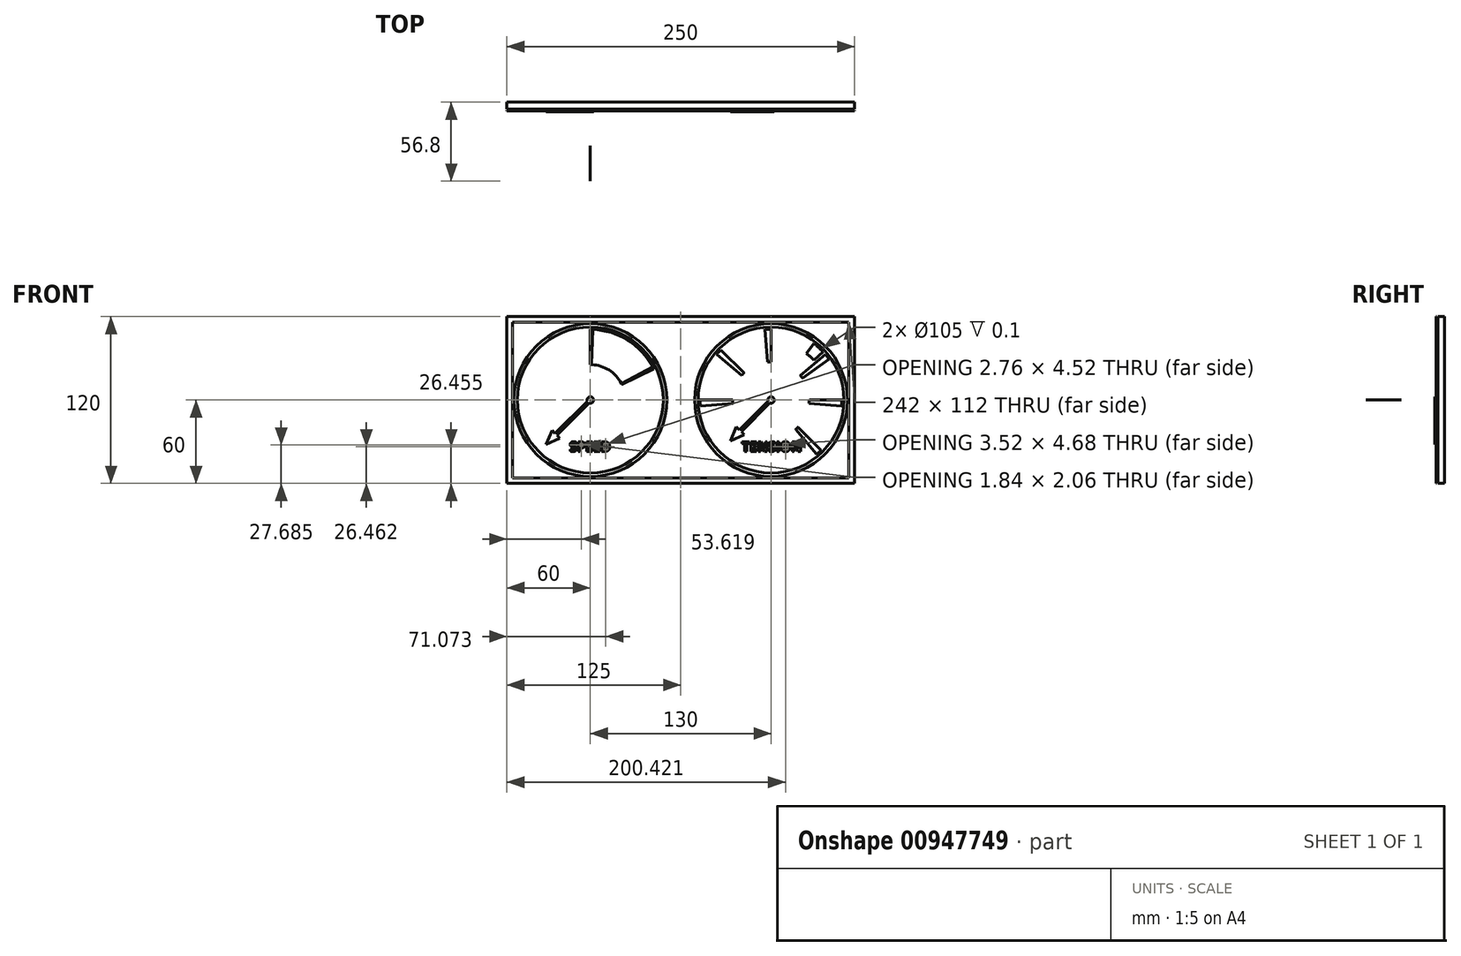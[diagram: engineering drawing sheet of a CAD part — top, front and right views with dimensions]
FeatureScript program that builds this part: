
annotation { "Feature Type Name" : "Feature", "Feature Type Description" : "" }
export const myFeature = defineFeature(function(context is Context, id is Id, definition is map)
    precondition{}
    {
        {
            var Q0;
            Q0=qCreatedBy(makeId("Right.planeOp"),FACE);
            var sketch = newSketch(context, id + "F0", { "sketchPlane" : qUnion([Q0])});
            skLineSegment(sketch, "E0", {"start": v(0, 0) * mm, "end": v(-116.06, 0) * mm, "construction": true});
            skSolve(sketch);
        }
        {
            var Q0;
            Q0=qCreatedBy(makeId("Right.planeOp"),FACE);
            var Q1;
            Q1=sQuery(id+"F0.wireOp",EDGE,"E0");
            cPlane(context, id + "F1", {"entities" : qUnion([Q0, Q1]), "cplaneType" : CPlaneType.LINE_ANGLE, "offset" : 25 * mm, "angle" : 135 * degree, "width" : 150 * mm, "height" : 150 * mm});
        }
        {
            var Q0;
            Q0=qCreatedBy(id+"F1.planeOp",FACE);
            var sketch = newSketch(context, id + "F2", { "sketchPlane" : qUnion([Q0])});
            skLineSegment(sketch, "E1.bottom", {"start": v(-25.4, 0) * mm, "end": v(-50.8, 0) * mm});
            skLineSegment(sketch, "E1.top", {"start": v(-25.4, 0) * mm, "end": v(-50.8, 0) * mm});
            skLineSegment(sketch, "E1.left", {"start": v(-25.4, 0) * mm, "end": v(-25.4, 0) * mm});
            skLineSegment(sketch, "E1.right", {"start": v(-50.8, 0) * mm, "end": v(-50.8, 0) * mm});
            skSolve(sketch);
        }
        {
            var Q0;
            Q0=qSketchRegion(id+"F2",true);
            var Q1;
            Q1=sQuery(id+"F0.wireOp",EDGE,"E0");
            revolve(context, id + "F3", {"surfaceOperationType" : NewSurfaceOperationType.NEW, "entities" : qUnion([Q0]), "axis" : qUnion([Q1]), "revolveType" : RevolveType.ONE_DIRECTION, "oppositeDirection" : true, "angle" : 135 * degree});
        }
        {
            var Q0;
            Q0=qCreatedBy(makeId("Right.planeOp"),FACE);
            var sketch = newSketch(context, id + "F4", { "sketchPlane" : qUnion([Q0])});
            skLineSegment(sketch, "E2.bottom", {"start": v(-0.01, 50.8) * mm, "end": v(0, 50.8) * mm});
            skLineSegment(sketch, "E2.top", {"start": v(0, 25.4) * mm, "end": v(0, 25.4) * mm});
            skLineSegment(sketch, "E2.left", {"start": v(-0.01, 50.8) * mm, "end": v(0, 25.4) * mm});
            skLineSegment(sketch, "E2.right", {"start": v(0, 50.8) * mm, "end": v(0, 25.4) * mm});
            skSolve(sketch);
        }
        {
            var Q0;
            Q0=qSketchRegion(id+"F4",true);
            var Q1;
            Q1=sQuery(id+"F0.wireOp",EDGE,"E0");
            revolve(context, id + "F5", {"surfaceOperationType" : NewSurfaceOperationType.NEW, "entities" : qUnion([Q0]), "axis" : qUnion([Q1]), "revolveType" : RevolveType.ONE_DIRECTION, "oppositeDirection" : true, "angle" : 2 * degree});
        }
        {
            var Q0;
            Q0=qCreatedBy(makeId("Right.planeOp"),FACE);
            var Q1;
            Q1=sQuery(id+"F0.wireOp",EDGE,"E0");
            cPlane(context, id + "F6", {"entities" : qUnion([Q0, Q1]), "cplaneType" : CPlaneType.LINE_ANGLE, "offset" : 25 * mm, "angle" : 2 * degree, "oppositeDirection" : true, "width" : 150 * mm, "height" : 150 * mm});
        }
        {
            var Q0;
            Q0=qCreatedBy(id+"F6.planeOp",FACE);
            var sketch = newSketch(context, id + "F7", { "sketchPlane" : qUnion([Q0])});
            skLineSegment(sketch, "E3.bottom", {"start": v(0, 50.8) * mm, "end": v(0, 50.8) * mm});
            skLineSegment(sketch, "E3.top", {"start": v(0, 25.4) * mm, "end": v(0, 25.4) * mm});
            skLineSegment(sketch, "E3.left", {"start": v(0, 50.8) * mm, "end": v(0, 25.4) * mm});
            skLineSegment(sketch, "E3.right", {"start": v(0, 50.8) * mm, "end": v(0, 25.4) * mm});
            skSolve(sketch);
        }
        {
            var Q0;
            Q0=qSketchRegion(id+"F7",true);
            var Q1;
            Q1=sQuery(id+"F0.wireOp",EDGE,"E0");
            revolve(context, id + "F8", {"surfaceOperationType" : NewSurfaceOperationType.NEW, "entities" : qUnion([Q0]), "axis" : qUnion([Q1]), "revolveType" : RevolveType.ONE_DIRECTION, "oppositeDirection" : true, "angle" : 60 * degree});
        }
        {
            var Q0;
            Q0=qCreatedBy(id+"F6.planeOp",FACE);
            var Q1;
            Q1=sQuery(id+"F0.wireOp",EDGE,"E0");
            cPlane(context, id + "F9", {"entities" : qUnion([Q0, Q1]), "cplaneType" : CPlaneType.LINE_ANGLE, "offset" : 25 * mm, "angle" : 60 * degree, "oppositeDirection" : true, "width" : 150 * mm, "height" : 150 * mm});
        }
        {
            var Q0;
            Q0=qCreatedBy(id+"F9.planeOp",FACE);
            var sketch = newSketch(context, id + "F10", { "sketchPlane" : qUnion([Q0])});
            skLineSegment(sketch, "E4.bottom", {"start": v(50.8, 0) * mm, "end": v(25.4, 0) * mm});
            skLineSegment(sketch, "E4.top", {"start": v(50.8, 0) * mm, "end": v(25.4, -0.01) * mm});
            skLineSegment(sketch, "E4.left", {"start": v(50.8, 0) * mm, "end": v(50.8, 0) * mm});
            skLineSegment(sketch, "E4.right", {"start": v(25.4, 0) * mm, "end": v(25.4, -0.01) * mm});
            skSolve(sketch);
        }
        {
            var Q0;
            Q0=qSketchRegion(id+"F10",true);
            var Q1;
            Q1=sQuery(id+"F0.wireOp",EDGE,"E0");
            revolve(context, id + "F11", {"surfaceOperationType" : NewSurfaceOperationType.NEW, "entities" : qUnion([Q0]), "axis" : qUnion([Q1]), "revolveType" : RevolveType.ONE_DIRECTION, "oppositeDirection" : true, "angle" : 2 * degree});
        }
        {
            var Q0;
            Q0=qCreatedBy(makeId("Front.planeOp"),FACE);
            var sketch = newSketch(context, id + "F12", { "sketchPlane" : qUnion([Q0])});
            skLineSegment(sketch, "E5.bottom", {"start": v(-0.77, -2.19) * mm, "end": v(-24.04, -25.46) * mm});
            skLineSegment(sketch, "E5.top", {"start": v(-2.19, -0.77) * mm, "end": v(-25.46, -24.04) * mm});
            skPoint(sketch, "E5.middle", {"position": v(0, 0) * mm});
            skLineSegment(sketch, "E6", {"start": v(0, 0) * mm, "end": v(0, 10.99) * mm, "construction": true});
            skPoint(sketch, "E7", {"position": v(-24.75, -24.75) * mm});
            skCircle(sketch, "E8", {"center": v(-24.75, -24.75) * mm, "radius": 10.19 * mm, "construction": true});
            skLineSegment(sketch, "E9", {"start": v(-24.04, -25.46) * mm, "end": v(-21.92, -27.58) * mm});
            skLineSegment(sketch, "E10", {"start": v(-25.46, -24.04) * mm, "end": v(-27.58, -21.92) * mm});
            skLineSegment(sketch, "E11", {"start": v(-24.75, -24.75) * mm, "end": v(-31.95, -31.95) * mm, "construction": true});
            skLineSegment(sketch, "E12", {"start": v(-31.95, -31.95) * mm, "end": v(-27.58, -21.92) * mm});
            skLineSegment(sketch, "E13", {"start": v(-21.92, -27.58) * mm, "end": v(-31.95, -31.95) * mm});
            skArc(sketch, "E14", {"start": v(-0.77, -2.19) * mm, "mid": v(1.64, 1.64) * mm, "end": v(-2.19, -0.77) * mm});
            skPoint(sketch, "E15.orphan", {"position": v(-0.7, 0.7) * mm});
            skPoint(sketch, "E16.end.orphan", {"position": v(0.7, -0.7) * mm});
            skSolve(sketch);
        }
        {
            var Q0;
            Q0=qSketchRegion(id+"F12",true);
            extrude(context, id + "F13", {"entities" : qUnion([Q0]), "depth" : 1 * mm, "offsetDistance" : 25 * mm});
        }
        {
            var Q0;
            Q0=qCreatedBy(makeId("Front.planeOp"),FACE);
            var sketch = newSketch(context, id + "F14", { "sketchPlane" : qUnion([Q0])});
            skCircle(sketch, "E17", {"center": v(0, 0) * mm, "radius": 52.5 * mm});
            skCircle(sketch, "E18", {"center": v(0, 0) * mm, "radius": 55 * mm});
            skSolve(sketch);
        }
        {
            var Q0;
            Q0=qSketchRegion(id+"F14",true);
            extrude(context, id + "F15", {"entities" : qUnion([Q0]), "depth" : .1 * mm, "offsetDistance" : 25 * mm});
        }
        {
            var Q0;
            Q0=qCreatedBy(makeId("Front.planeOp"),FACE);
            var sketch = newSketch(context, id + "F16", { "sketchPlane" : qUnion([Q0])});
            skCircle(sketch, "E19", {"center": v(130, 0) * mm, "radius": 52.5 * mm});
            skCircle(sketch, "E20", {"center": v(130, 0) * mm, "radius": 55 * mm});
            skSolve(sketch);
        }
        {
            var Q0;
            Q0=qSketchRegion(id+"F16",true);
            extrude(context, id + "F17", {"entities" : qUnion([Q0]), "depth" : .1 * mm, "offsetDistance" : 25 * mm});
        }
        {
            var Q0;
            Q0=qCreatedBy(makeId("Front.planeOp"),FACE);
            var sketch = newSketch(context, id + "F18", { "sketchPlane" : qUnion([Q0])});
            skArc(sketch, "E21", {"start": v(79.2, -4.44) * mm, "mid": v(79.05, -2.22) * mm, "end": v(79, 0) * mm});
            skLineSegment(sketch, "E22", {"start": v(79, 0) * mm, "end": v(102.5, 0) * mm});
            skLineSegment(sketch, "E23", {"start": v(102.6, -2.4) * mm, "end": v(79.2, -4.44) * mm});
            skArc(sketch, "E24", {"start": v(102.5, 0) * mm, "mid": v(102.53, -1.2) * mm, "end": v(102.6, -2.4) * mm});
            skSolve(sketch);
        }
        {
            var Q0;
            Q0=qSketchRegion(id+"F18",true);
            extrude(context, id + "F19", {"entities" : qUnion([Q0]), "depth" : .1 * mm, "offsetDistance" : 25 * mm});
        }
        {
            var Q0;
            Q0=qCreatedBy(makeId("Front.planeOp"),FACE);
            var sketch = newSketch(context, id + "F20", { "sketchPlane" : qUnion([Q0])});
            skLineSegment(sketch, "E25", {"start": v(130, 0) * mm, "end": v(223.12, 0) * mm, "construction": true});
            skLineSegment(sketch, "E26", {"start": v(147.68, -21.07) * mm, "end": v(162.78, -39.07) * mm});
            skArc(sketch, "E27", {"start": v(147.68, -21.07) * mm, "mid": v(148.58, -20.28) * mm, "end": v(149.45, -19.45) * mm});
            skArc(sketch, "E28", {"start": v(162.78, -39.07) * mm, "mid": v(164.46, -37.6) * mm, "end": v(166.06, -36.06) * mm});
            skLineSegment(sketch, "E29", {"start": v(149.45, -19.45) * mm, "end": v(166.06, -36.06) * mm});
            skSolve(sketch);
        }
        {
            var Q0;
            Q0=qSketchRegion(id+"F20",true);
            extrude(context, id + "F21", {"entities" : qUnion([Q0]), "depth" : .1 * mm, "offsetDistance" : 25 * mm});
        }
        {
            var Q0;
            Q0=qCreatedBy(makeId("Front.planeOp"),FACE);
            var sketch = newSketch(context, id + "F22", { "sketchPlane" : qUnion([Q0])});
            skLineSegment(sketch, "E30", {"start": v(130, 27.5) * mm, "end": v(130, 51) * mm});
            skLineSegment(sketch, "E31", {"start": v(127.6, 27.4) * mm, "end": v(125.56, 50.8) * mm});
            skArc(sketch, "E32", {"start": v(127.6, 27.4) * mm, "mid": v(128.8, 27.47) * mm, "end": v(130, 27.5) * mm});
            skArc(sketch, "E33", {"start": v(125.56, 50.8) * mm, "mid": v(127.78, 50.95) * mm, "end": v(130, 51) * mm});
            skSolve(sketch);
        }
        {
            var Q0;
            Q0=qSketchRegion(id+"F22",true);
            extrude(context, id + "F23", {"entities" : qUnion([Q0]), "depth" : .1 * mm, "offsetDistance" : 25 * mm});
        }
        {
            var Q0;
            Q0=qCreatedBy(makeId("Front.planeOp"),FACE);
            var sketch = newSketch(context, id + "F24", { "sketchPlane" : qUnion([Q0])});
            skLineSegment(sketch, "E34", {"start": v(110.55, 19.45) * mm, "end": v(93.94, 36.06) * mm});
            skLineSegment(sketch, "E35", {"start": v(130, 0) * mm, "end": v(130, 16.9) * mm, "construction": true});
            skLineSegment(sketch, "E36", {"start": v(108.93, 17.68) * mm, "end": v(90.93, 32.78) * mm});
            skArc(sketch, "E37", {"start": v(93.94, 36.06) * mm, "mid": v(92.4, 34.46) * mm, "end": v(90.93, 32.78) * mm});
            skArc(sketch, "E38", {"start": v(110.55, 19.45) * mm, "mid": v(109.72, 18.58) * mm, "end": v(108.93, 17.68) * mm});
            skSolve(sketch);
        }
        {
            var Q0;
            Q0=qSketchRegion(id+"F24",true);
            extrude(context, id + "F25", {"entities" : qUnion([Q0]), "depth" : .1 * mm, "offsetDistance" : 25 * mm});
        }
        {
            var Q0;
            Q0=qCreatedBy(makeId("Front.planeOp"),FACE);
            var sketch = newSketch(context, id + "F26", { "sketchPlane" : qUnion([Q0])});
            skLineSegment(sketch, "E39", {"start": v(151.07, 17.68) * mm, "end": v(169.07, 32.78) * mm});
            skLineSegment(sketch, "E40", {"start": v(130, 0) * mm, "end": v(130, 13.97) * mm, "construction": true});
            skLineSegment(sketch, "E41", {"start": v(152.53, 15.77) * mm, "end": v(171.78, 29.25) * mm});
            skArc(sketch, "E42", {"start": v(151.07, 17.68) * mm, "mid": v(151.82, 16.74) * mm, "end": v(152.53, 15.77) * mm});
            skArc(sketch, "E43", {"start": v(169.07, 32.78) * mm, "mid": v(170.46, 31.05) * mm, "end": v(171.78, 29.25) * mm});
            skSolve(sketch);
        }
        {
            var Q0;
            Q0=qSketchRegion(id+"F26",true);
            extrude(context, id + "F27", {"entities" : qUnion([Q0]), "depth" : .1 * mm, "offsetDistance" : 25 * mm});
        }
        {
            var Q0;
            Q0=qCreatedBy(makeId("Front.planeOp"),FACE);
            var sketch = newSketch(context, id + "F28", { "sketchPlane" : qUnion([Q0])});
            skLineSegment(sketch, "E44", {"start": v(157.5, 0) * mm, "end": v(181, 0) * mm});
            skLineSegment(sketch, "E45", {"start": v(157.4, -2.4) * mm, "end": v(180.8, -4.44) * mm});
            skArc(sketch, "E46", {"start": v(181, 0) * mm, "mid": v(180.95, -2.22) * mm, "end": v(180.8, -4.44) * mm});
            skArc(sketch, "E47", {"start": v(157.5, 0) * mm, "mid": v(157.47, -1.2) * mm, "end": v(157.4, -2.4) * mm});
            skSolve(sketch);
        }
        {
            var Q0;
            Q0=qSketchRegion(id+"F28",true);
            extrude(context, id + "F29", {"entities" : qUnion([Q0]), "depth" : .1 * mm, "offsetDistance" : 25 * mm});
        }
        {
            var Q0;
            Q0=qCreatedBy(makeId("Front.planeOp"),FACE);
            var sketch = newSketch(context, id + "F30", { "sketchPlane" : qUnion([Q0])});
            skLineSegment(sketch, "E48", {"start": v(160.77, 28.58) * mm, "end": v(167.37, 34.7) * mm});
            skLineSegment(sketch, "E49", {"start": v(155.34, 33.5) * mm, "end": v(160.77, 40.67) * mm});
            skArc(sketch, "E50", {"start": v(167.37, 34.7) * mm, "mid": v(164.2, 37.83) * mm, "end": v(160.77, 40.67) * mm});
            skArc(sketch, "E51", {"start": v(160.77, 28.58) * mm, "mid": v(158.17, 31.16) * mm, "end": v(155.34, 33.5) * mm});
            skSolve(sketch);
        }
        {
            var Q0;
            Q0=qSketchRegion(id+"F30",true);
            extrude(context, id + "F31", {"entities" : qUnion([Q0]), "depth" : .1 * mm, "offsetDistance" : 25 * mm});
        }
        {
            var Q0;
            Q0=qCreatedBy(makeId("Front.planeOp"),FACE);
            var sketch = newSketch(context, id + "F32", { "sketchPlane" : qUnion([Q0])});
            skLineSegment(sketch, "E52.bottom", {"start": v(129.23, -2.19) * mm, "end": v(108.62, -22.8) * mm});
            skLineSegment(sketch, "E52.top", {"start": v(127.81, -0.77) * mm, "end": v(107.2, -21.38) * mm});
            skPoint(sketch, "E52.middle", {"position": v(130, 0) * mm});
            skLineSegment(sketch, "E53", {"start": v(130, 0) * mm, "end": v(130, 10.99) * mm, "construction": true});
            skPoint(sketch, "E54", {"position": v(107.9, -22.1) * mm});
            skCircle(sketch, "E55", {"center": v(107.9, -22.1) * mm, "radius": 10.19 * mm, "construction": true});
            skLineSegment(sketch, "E56", {"start": v(108.62, -22.8) * mm, "end": v(110.74, -24.92) * mm});
            skLineSegment(sketch, "E57", {"start": v(107.2, -21.38) * mm, "end": v(105.08, -19.26) * mm});
            skLineSegment(sketch, "E58", {"start": v(107.9, -22.1) * mm, "end": v(100.7, -29.3) * mm, "construction": true});
            skLineSegment(sketch, "E59", {"start": v(100.7, -29.3) * mm, "end": v(105.08, -19.26) * mm});
            skLineSegment(sketch, "E60", {"start": v(110.74, -24.92) * mm, "end": v(100.7, -29.3) * mm});
            skArc(sketch, "E61", {"start": v(129.23, -2.19) * mm, "mid": v(131.64, 1.64) * mm, "end": v(127.81, -0.77) * mm});
            skPoint(sketch, "E62.orphan", {"position": v(129.3, 0.7) * mm});
            skPoint(sketch, "E63.end.orphan", {"position": v(130.7, -0.7) * mm});
            skSolve(sketch);
        }
        {
            var Q0;
            Q0=qSketchRegion(id+"F32",true);
            extrude(context, id + "F33", {"entities" : qUnion([Q0]), "depth" : 1 * mm, "offsetDistance" : 25 * mm});
        }
        {
            var Q0;
            Q0=qCreatedBy(makeId("Front.planeOp"),FACE);
            var sketch = newSketch(context, id + "F34", { "sketchPlane" : qUnion([Q0])});
            skLineSegment(sketch, "E64", {"start": v(0, 0) * mm, "end": v(130, 0) * mm, "construction": true});
            skLineSegment(sketch, "E65.bottom", {"start": v(186, -56) * mm, "end": v(-56, -56) * mm});
            skLineSegment(sketch, "E65.top", {"start": v(186, 56) * mm, "end": v(-56, 56) * mm});
            skLineSegment(sketch, "E65.left", {"start": v(186, -56) * mm, "end": v(186, 56) * mm});
            skLineSegment(sketch, "E65.right", {"start": v(-56, -56) * mm, "end": v(-56, 56) * mm});
            skPoint(sketch, "E65.middle", {"position": v(65, 0) * mm});
            skLineSegment(sketch, "E66.bottom", {"start": v(190, -60) * mm, "end": v(-60, -60) * mm});
            skLineSegment(sketch, "E66.top", {"start": v(190, 60) * mm, "end": v(-60, 60) * mm});
            skLineSegment(sketch, "E66.left", {"start": v(190, -60) * mm, "end": v(190, 60) * mm});
            skLineSegment(sketch, "E66.right", {"start": v(-60, -60) * mm, "end": v(-60, 60) * mm});
            skText(sketch, "E67", { "text": "SPEED", "fontName": "OpenSans-Bold.ttf"});
            skText(sketch, "E68", { "text": "TENSION", "fontName": "OpenSans-Regular.ttf"});
            skLineSegment(sketch, "E69", {"start": v(-15.3, -30.02) * mm, "end": v(165.4, -30.02) * mm, "construction": true});
            const initialGuessF34  = {"E67": [-0.0153, -0.03702, 1, 0, 0.007], "E68": [0.10955, -0.03702, 1, 0, 0.007]};
            skSetInitialGuess(sketch, initialGuessF34);
            skSolve(sketch);
        }
        {
            var Q0;
            Q0=qSketchRegion(id+"F34",true);
            extrude(context, id + "F35", {"entities" : qUnion([Q0]), "depth" : .1 * mm, "offsetDistance" : 25 * mm});
        }
        {
            var Q0;
            Q0=qCreatedBy(makeId("Front.planeOp"),FACE);
            var sketch = newSketch(context, id + "F36", { "sketchPlane" : qUnion([Q0])});
            skLineSegment(sketch, "E70", {"start": v(3.26, -76.77) * mm, "end": v(133.26, -76.77) * mm, "construction": true});
            skPoint(sketch, "E71.middle", {"position": v(68.26, -76.77) * mm});
            skText(sketch, "E72", { "text": "SPEED", "fontName": "OpenSans-Bold.ttf"});
            skText(sketch, "E73", { "text": "TENSION", "fontName": "OpenSans-Bold.ttf"});
            skLineSegment(sketch, "E74", {"start": v(-15, -30.02) * mm, "end": v(168.67, -30.02) * mm, "construction": true});
            skPoint(sketch, "E75", {"position": v(76.84, -30.02) * mm});
            skLineSegment(sketch, "E76", {"start": v(0, 0) * mm, "end": v(0, -24.7) * mm, "construction": true});
            const initialGuessF36  = {"E72": [-0.015, -0.03702, 1, 0, 0.007], "E73": [0.109, -0.03702, 1, 0, 0.007]};
            skSetInitialGuess(sketch, initialGuessF36);
            skSolve(sketch);
        }
        {
            var Q0;
            Q0=qSketchRegion(id+"F36",true);
            extrude(context, id + "F37", {"entities" : qUnion([Q0]), "depth" : .1 * mm, "offsetDistance" : 25 * mm});
        }
        {
            var Q0;
            Q0=qCreatedBy(makeId("Front.planeOp"),FACE);
            var sketch = newSketch(context, id + "F38", { "sketchPlane" : qUnion([Q0])});
            skLineSegment(sketch, "E77.bottom", {"start": v(-60, 60) * mm, "end": v(190, 60) * mm});
            skLineSegment(sketch, "E77.top", {"start": v(-60, -60) * mm, "end": v(190, -60) * mm});
            skLineSegment(sketch, "E77.left", {"start": v(-60, 60) * mm, "end": v(-60, -60) * mm});
            skLineSegment(sketch, "E77.right", {"start": v(190, 60) * mm, "end": v(190, -60) * mm});
            skSolve(sketch);
        }
        {
            var Q0;
            Q0=qSketchRegion(id+"F38",true);
            extrude(context, id + "F39", {"entities" : qUnion([Q0]), "oppositeDirection" : true, "depth" : 5 * mm, "offsetDistance" : 25 * mm});
        }
        {
            var Q0;
            Q0=makeQuery(id+"F39.opExtrude","SWEPT_BODY",BODY,{"disambiguationData":[OSD([sQuery(id+"F38.wireOp",EDGE,"E77.bottom"),sQuery(id+"F38.wireOp",EDGE,"E77.top"),sQuery(id+"F38.wireOp",EDGE,"E77.left"),sQuery(id+"F38.wireOp",EDGE,"E77.right")])]});
            transform(context, id + "F40", {"entities" : qUnion([Q0]), "transformType" : TransformType.TRANSLATION_3D, "dx" : 0 * mm, "dy" : 1 * mm, "dz" : 0 * mm, "makeCopy" : false});
        }
    });
